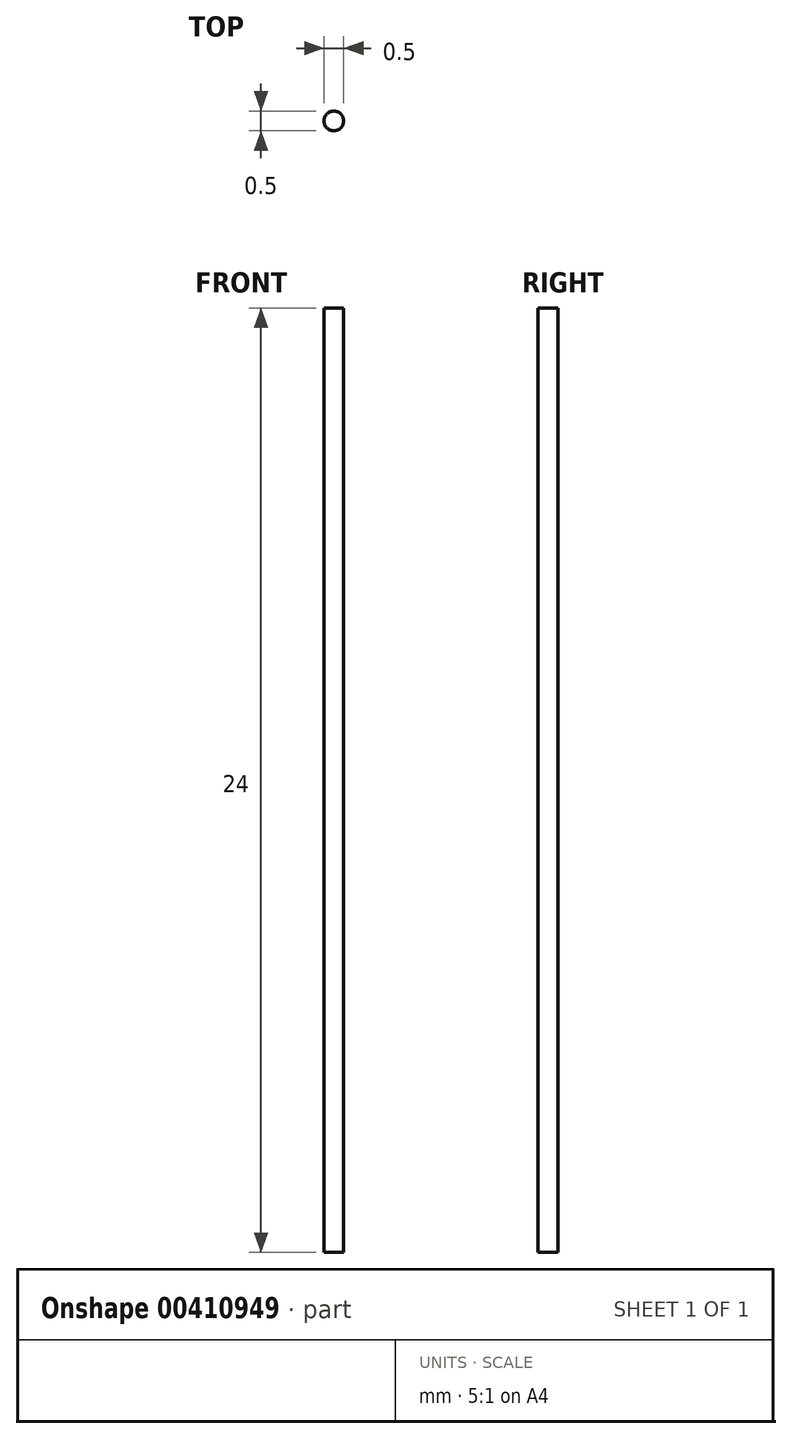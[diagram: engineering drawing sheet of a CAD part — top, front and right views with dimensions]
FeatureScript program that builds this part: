
annotation { "Feature Type Name" : "Feature", "Feature Type Description" : "" }
export const myFeature = defineFeature(function(context is Context, id is Id, definition is map)
    precondition{}
    {
        {
            var Q0;
            Q0=qCreatedBy(makeId("Top.planeOp"),FACE);
            var sketch = newSketch(context, id + "F0", { "sketchPlane" : qUnion([Q0])});
            skCircle(sketch, "E0", {"center": v(0, 0) * mm, "radius": 0.25 * mm});
            skSolve(sketch);
        }
        {
            var Q0;
            Q0=makeQuery(id+"F0.imprint","IMPRINT",FACE,{"disambiguationData":[TD([[makeQuery(id+"F0.imprint","IMPRINT",EDGE,{"derivedFrom":sQuery(id+"F0.wireOp",EDGE,"E0")}),1.0]])]});
            extrude(context, id + "F1", {"entities" : qUnion([Q0]), "depth" : 24 * mm});
        }
    });
